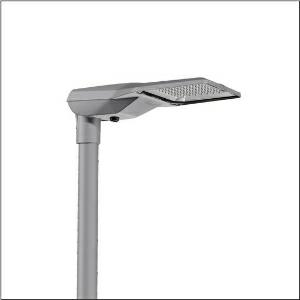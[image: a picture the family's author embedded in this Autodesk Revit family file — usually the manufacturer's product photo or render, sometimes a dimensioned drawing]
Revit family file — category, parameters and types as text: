
# Revit family: streetlight_sl_21_iq_midi___p0_8a_5xe3u31u08nb_8349
name_source: partatom
category: Lighting Fixtures
units: mm (PartAtom-declared; Revit-internal decimal feet)

## family parameters
Cut with Voids When Loaded = No
Host = Face
Light Source = No
Part Type = Normal
Room Calculation Point = No
Round Connector Dimension = Use Diameter
Shared = No

## types (1)
- --- (1 x LED, 21740 lm, 136.6 W, 3000K)
    Apparent Load = 137 VA
    CIE Flux Codes = 36 69 97 100 100
    Color Rendering = 70
    Color Temperature = 3000K
    Default Elevation = 1800 mm
    Description = Streetlight SL 21 iQ midi, mast luminaire, primary light control with lens, of PMMA, primary optical cover: cover, of toughened safety glass, transparent, light distribution: P0.8a, light emission: direct distribution, primary light characteristic: asymmetric, installation type: post-top, side-entry, LED, High Power LED, rated luminous flux: 21.740lm, luminous efficacy: 159lm/W, light colour: 730, colour temperature: 3000K, control gear: iQ-Street Remote, D4i with power reduction, control: pre-setting: logarithmic dimming characteristic, Street-Remote, Auto-Match, Temp-Guard, Lumen-Switch, Night-Set, Smart-Wire, Light-Fading, Desk-Remote (wireless, voltage-free reading and setting of iQ features in the workshop via application-optimized NFC function/RFID function), optimised constant luminous flux control (CLO 2.0), mains connection: 230..240V, AC, 50/60Hz, start of lifetime: 137W, end of service life: 144W, reduction: 61W, luminaire housing, of diecast aluminium, powder-coated, Siteco® metallic grey (DB 702S), corrosivity category C5 mid according to DIN EN ISO 12944, please order mast flange separately, inclination adjustable: 0°, 5°, 10°, 15°, sealing non-destructively replaceable, multi-level sealing system, length: 644mm, width: 335mm, height: 110mm, mast flange for spigot size: 42mm (side-entry): 5XC10008XM4, 60/48mm (side-entry/post-top): 5XC10108XM2, 76/60mm (side-entry/post-top): 5XC10108XM1, mounting height: 4..8m, Smart Interface below, protection rating (complete): IP66, insulation class (complete): insulation class II (safety insulation), certification: CE, ENEC, ENEC+, VDE, impact resistance: IK10, permissible operating ambient temperature for outdoor applications: -40..+50°C, standard-compliant lighting for roads and squares, packaging unit: 1 piece

Light Distribution: P0.8a
    Height = 111 mm
    Lamp = 1 x LED
    Lamp Light Flux = 21740 lm
    Lamp Power = 136.6 W
    Lamp count = 1
    Length = 644 mm
    Luminous efficacy = 159 lm/W
    Manufacturer = Siteco
    ModVariant = No
    Model = 5XE3U31U08NB
    Number of Poles = 1
    OnlyDefault = Yes
    Power Factor = 1
    Product Name = Streetlight SL 21 iQ midi | P0.8a
    Product group = mast luminaire | pylon top
    ProductGroupID = 6100
    Protection Class = Protection class II
    Protection Degree = IP 66
    RLX_Detail_Level = 1
    RLX_Emergency_Light_Flux = 0 lm
    RLX_Emergency_Type = 0
    RLX_Emergency_Type_DB = No
    RlxData = <blob elided: 27057 chars, md5=035ae4b0>
    Socket = socket
    Standby Power = 0 W
    System Light Flux = 21740 lm
    System Power = 137 W
    Type Comments = factory setting: luminous flux: 100 % | dim-lin: 254 | 733 mA
    Type Image = l_1004300.jpg
    URL = http://relux.com
    VarID = @adj_072060
    Voltage = 0 V
    Weight = 0.00 kg
    Width = 336 mm

## geometry (parser evidence)
native form markers: Blend x4, Sweep x12
no freeform markers — native parametric forms only
